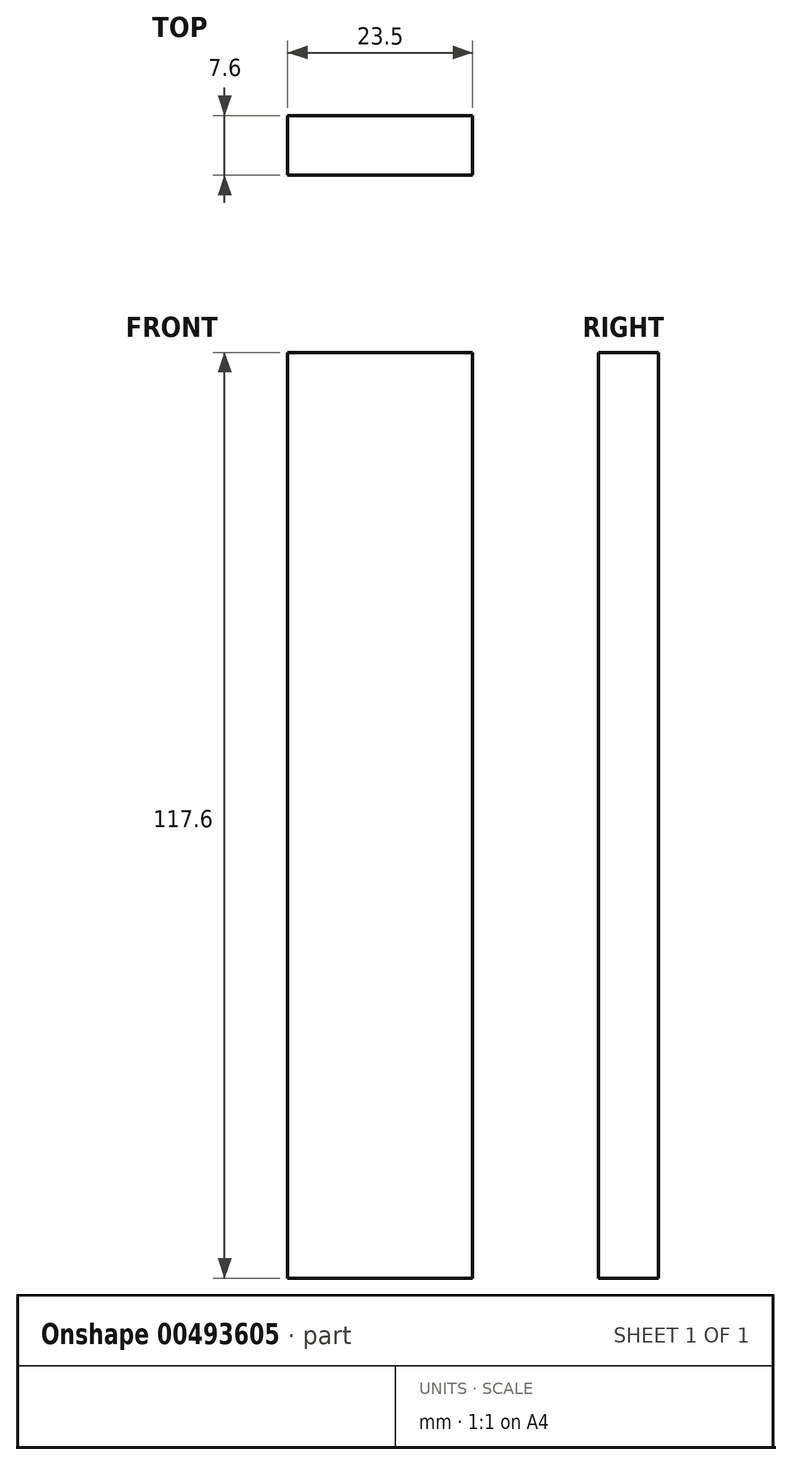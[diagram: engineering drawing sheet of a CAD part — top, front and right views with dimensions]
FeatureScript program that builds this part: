
annotation { "Feature Type Name" : "Feature", "Feature Type Description" : "" }
export const myFeature = defineFeature(function(context is Context, id is Id, definition is map)
    precondition{}
    {
        {
            var Q0;
            Q0=qCreatedBy(makeId("Front.planeOp"),FACE);
            var sketch = newSketch(context, id + "F0", { "sketchPlane" : qUnion([Q0])});
            skLineSegment(sketch, "E0.bottom", {"start": v(-11.75, 58.8) * mm, "end": v(11.75, 58.8) * mm});
            skLineSegment(sketch, "E0.top", {"start": v(-11.75, -58.8) * mm, "end": v(11.75, -58.8) * mm});
            skLineSegment(sketch, "E0.left", {"start": v(-11.75, 58.8) * mm, "end": v(-11.75, -58.8) * mm});
            skLineSegment(sketch, "E0.right", {"start": v(11.75, 58.8) * mm, "end": v(11.75, -58.8) * mm});
            skPoint(sketch, "E0.middle", {"position": v(0, 0) * mm});
            skSolve(sketch);
        }
        {
            var Q0;
            Q0=makeQuery(id+"F0.imprint","IMPRINT",FACE,{"disambiguationData":[TD([[makeQuery(id+"F0.imprint","IMPRINT",EDGE,{"derivedFrom":sQuery(id+"F0.wireOp",EDGE,"E0.bottom")}),-1.0]])]});
            extrude(context, id + "F1", {"entities" : qUnion([Q0]), "endBound" : BoundingType.SYMMETRIC, "depth" : 7.6 * mm});
        }
    });
